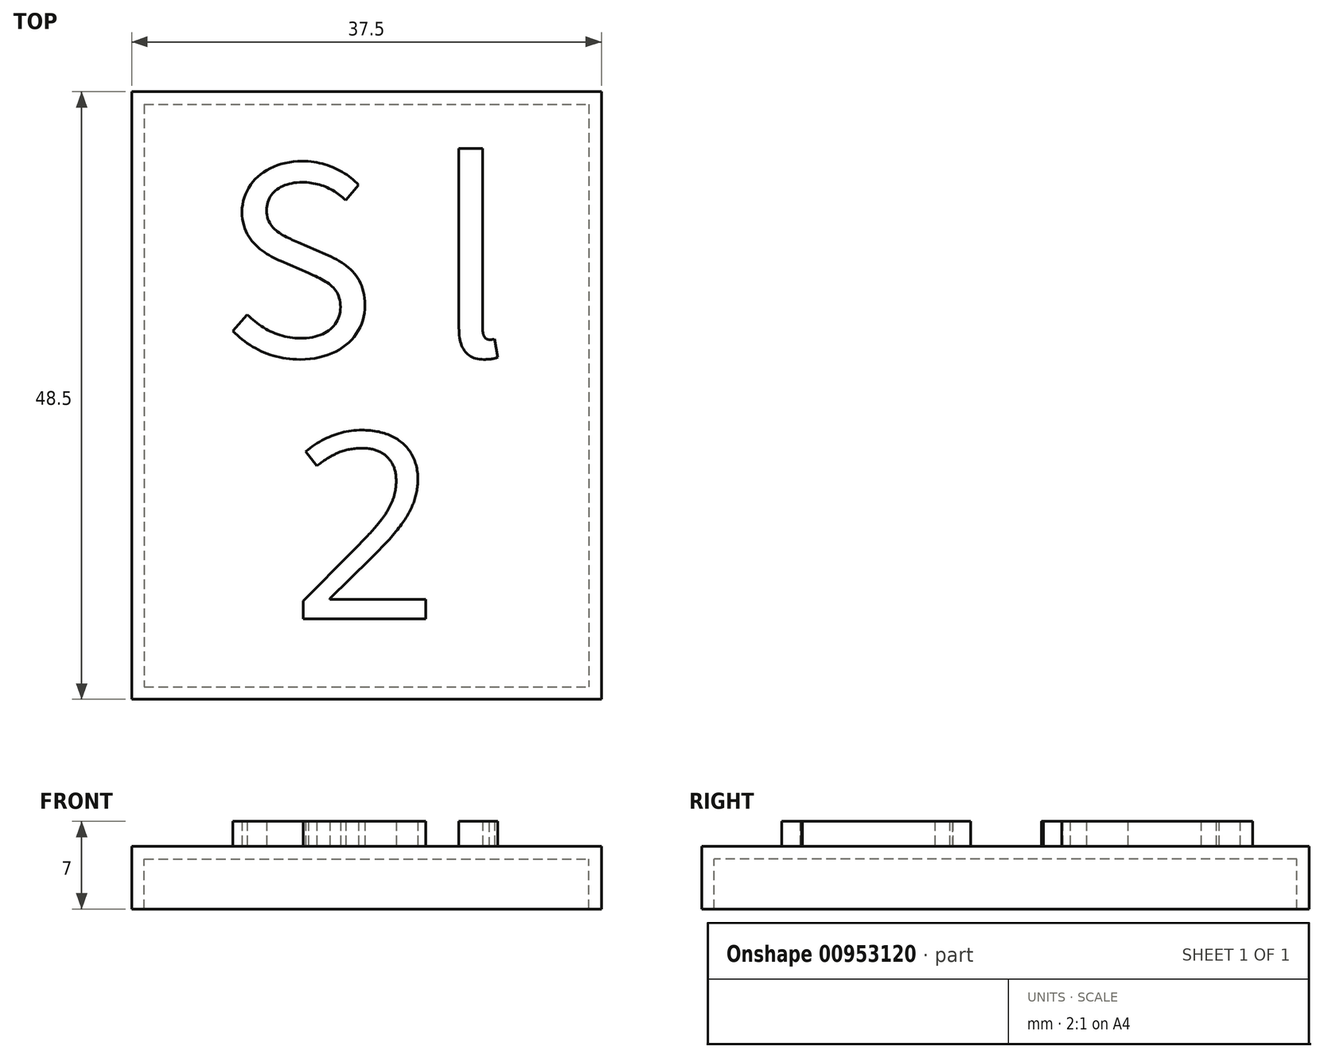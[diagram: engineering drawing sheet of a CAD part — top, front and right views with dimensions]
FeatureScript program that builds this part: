
annotation { "Feature Type Name" : "Feature", "Feature Type Description" : "" }
export const myFeature = defineFeature(function(context is Context, id is Id, definition is map)
    precondition{}
    {
        {
            var Q0;
            Q0=qCreatedBy(makeId("Top.planeOp"),FACE);
            var sketch = newSketch(context, id + "F0", { "sketchPlane" : qUnion([Q0])});
            skLineSegment(sketch, "E0.bottom", {"start": v(-17.75, 23.25) * mm, "end": v(17.75, 23.25) * mm});
            skLineSegment(sketch, "E0.top", {"start": v(-17.75, -23.25) * mm, "end": v(17.75, -23.25) * mm});
            skLineSegment(sketch, "E0.left", {"start": v(-17.75, 23.25) * mm, "end": v(-17.75, -23.25) * mm});
            skLineSegment(sketch, "E0.right", {"start": v(17.75, 23.25) * mm, "end": v(17.75, -23.25) * mm});
            skPoint(sketch, "E0.middle", {"position": v(0, 0) * mm});
            skText(sketch, "E1", { "text": "S l\n", "fontName": "NotoSansCJKtc-Regular.otf"});
            skLineSegment(sketch, "E2.bottom", {"start": v(-18.75, 24.25) * mm, "end": v(18.75, 24.25) * mm});
            skLineSegment(sketch, "E2.top", {"start": v(-18.75, -24.25) * mm, "end": v(18.75, -24.25) * mm});
            skLineSegment(sketch, "E2.left", {"start": v(-18.75, 24.25) * mm, "end": v(-18.75, -24.25) * mm});
            skLineSegment(sketch, "E2.right", {"start": v(18.75, 24.25) * mm, "end": v(18.75, -24.25) * mm});
            skText(sketch, "E3", { "text": "2\n", "fontName": "OpenSans-Regular.ttf"});
            const initialGuessF0  = {"E1": [-0.01165, 0.00315, 1, 0, 0.015], "E3": [-0.00607, -0.01785, 1, 0, 0.015]};
            skSetInitialGuess(sketch, initialGuessF0);
            skSolve(sketch);
        }
        {
            var Q0;
            Q0=makeQuery(id+"F0.imprint","IMPRINT",FACE,{"disambiguationData":[TD([[makeQuery(id+"F0.imprint","IMPRINT",EDGE,{"derivedFrom":sQuery(id+"F0.wireOp",EDGE,"E0.bottom")}),-1.0]])]});
            extrude(context, id + "F1", {"entities" : qUnion([Q0]), "depth" : 1 * mm, "offsetDistance" : 25 * mm});
        }
        {
            var Q0;
            Q0=makeQuery(id+"F0.imprint","IMPRINT",FACE,{"disambiguationData":[TD([[makeQuery(id+"F0.imprint","IMPRINT",EDGE,{"derivedFrom":sQuery(id+"F0.wireOp",EDGE,"E0.bottom")}),1.0]])]});
            extrude(context, id + "F2", {"entities" : qUnion([Q0]), "operationType" : NewBodyOperationType.ADD, "oppositeDirection" : true, "depth" : 4 * mm, "offsetDistance" : 25 * mm, "hasSecondDirection" : true, "secondDirectionOppositeDirection" : false, "secondDirectionDepth" : 1 * mm});
        }
        {
            var Q0;
            Q0=makeQuery(id+"F0.imprint","IMPRINT",FACE,{"disambiguationData":[TD([[makeQuery(id+"F0.imprint","IMPRINT",EDGE,{"derivedFrom":sQuery(id+"F0.wireOp",EDGE,"E1.sketch_text.stroke-25")}),-1.0]])]});
            var Q1;
            Q1=makeQuery(id+"F0.imprint","IMPRINT",FACE,{"disambiguationData":[TD([[makeQuery(id+"F0.imprint","IMPRINT",EDGE,{"derivedFrom":sQuery(id+"F0.wireOp",EDGE,"E1.sketch_text.stroke-0")}),1.0]])]});
            var Q2;
            Q2=makeQuery(id+"F0.imprint","IMPRINT",FACE,{"disambiguationData":[TD([[makeQuery(id+"F0.imprint","IMPRINT",EDGE,{"derivedFrom":sQuery(id+"F0.wireOp",EDGE,"E1.sketch_text.stroke-16")}),1.0]])]});
            var Q3;
            Q3=makeQuery(id+"F0.imprint","IMPRINT",FACE,{"disambiguationData":[TD([[makeQuery(id+"F0.imprint","IMPRINT",EDGE,{"derivedFrom":sQuery(id+"F0.wireOp",EDGE,"E3.sketch_text.stroke-0")}),-1.0]])]});
            extrude(context, id + "F3", {"entities" : qUnion([Q0, Q1, Q2, Q3]), "operationType" : NewBodyOperationType.ADD, "depth" : 3 * mm, "offsetDistance" : 25 * mm});
        }
        {
            var Q0;
            Q0=makeQuery(id+"F0.imprint","IMPRINT",FACE,{"disambiguationData":[TD([[makeQuery(id+"F0.imprint","IMPRINT",EDGE,{"derivedFrom":sQuery(id+"F0.wireOp",EDGE,"E3.sketch_text.stroke-0")}),-1.0]])]});
            extrude(context, id + "F4", {"entities" : qUnion([Q0]), "operationType" : NewBodyOperationType.ADD, "depth" : 3 * mm, "offsetDistance" : 25 * mm});
        }
    });
